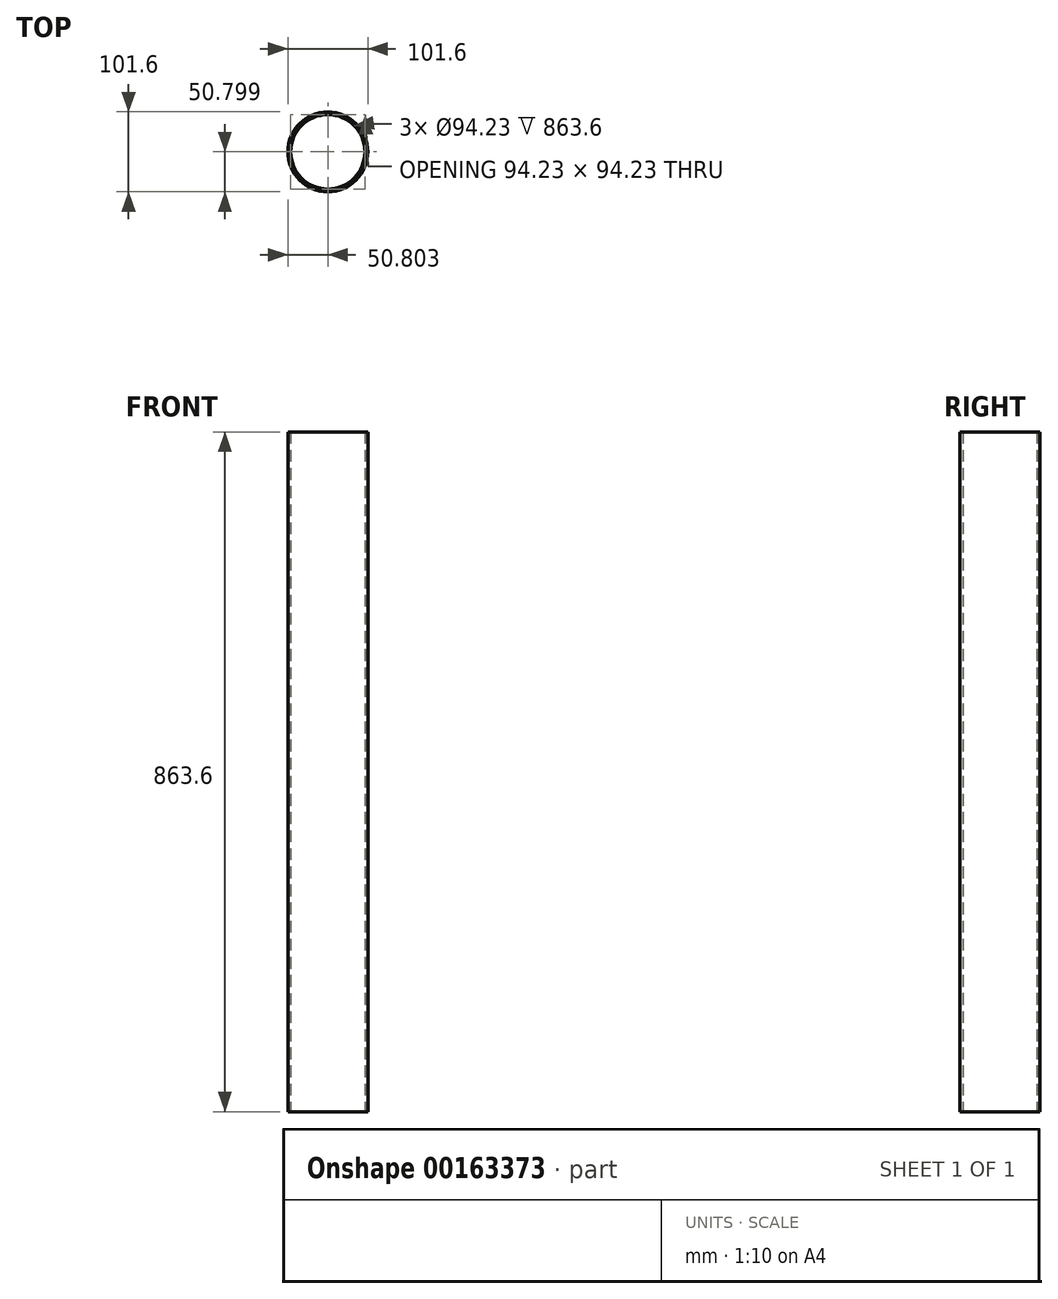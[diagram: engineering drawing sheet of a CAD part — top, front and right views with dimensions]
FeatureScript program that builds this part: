
annotation { "Feature Type Name" : "Feature", "Feature Type Description" : "" }
export const myFeature = defineFeature(function(context is Context, id is Id, definition is map)
    precondition{}
    {
        {
            var Q0;
            Q0=qCreatedBy(makeId("Top.planeOp"),FACE);
            var sketch = newSketch(context, id + "F0", { "sketchPlane" : qUnion([Q0])});
            skCircle(sketch, "E0", {"center": v(-54.95, -41.8) * mm, "radius": 50.8 * mm});
            skSolve(sketch);
        }
        {
            var Q0;
            Q0=makeQuery(id+"F0.imprint","IMPRINT",FACE,{"disambiguationData":[TD([[makeQuery(id+"F0.imprint","IMPRINT",EDGE,{"derivedFrom":sQuery(id+"F0.wireOp",EDGE,"E0")}),1.0]])]});
            extrude(context, id + "F1", {"entities" : qUnion([Q0]), "depth" : 863.6 * mm});
        }
        {
            var Q0;
            Q0=makeQuery(id+"F1.opExtrude","CAP_FACE",FACE,{"disambiguationData":[OSD([sQuery(id+"F0.wireOp",EDGE,"E0")])],"isStart":true});
            var sketch = newSketch(context, id + "F2", { "sketchPlane" : qUnion([Q0])});
            skCircle(sketch, "E1", {"center": v(-54.95, 41.8) * mm, "radius": 35.73 * mm});
            skSolve(sketch);
        }
        {
            var Q0;
            Q0=sQuery(id+"F2.wireOp",VERTEX,"E1.center");
            var Q1;
            Q1=makeQuery(id+"F1.opExtrude","SWEPT_BODY",BODY,{"disambiguationData":[OSD([sQuery(id+"F0.wireOp",EDGE,"E0")])]});
            hole(context, id + "F3", {"style" : HoleStyle.SIMPLE, "endStyle" : HoleEndStyle.THROUGH, "holeDiameter" : 94.23 * mm, "locations" : qUnion([Q0]), "scope" : qUnion([Q1]), "isTappedThrough" : true});
        }
    });
